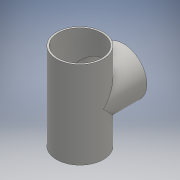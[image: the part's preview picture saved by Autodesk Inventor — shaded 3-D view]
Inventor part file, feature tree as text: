
AUTODESK INVENTOR PART (.ipt)
format: ipt  version: 2016 (Build 200138000, 138)  size: 144,896 bytes
history: native  units: mm
features: extrude x4, sketch x4, projected_geometry x1
ambient origin geometry x8: Origin, YZ Plane, XZ Plane, XY Plane, X Axis, Y Axis, Z Axis, Center Point
bodies: Solid1 (feature_tree)
feature tree (9):
  extrude  "Extrusion1"  Depth=9.52mm
  extrude  "Extrusion2"  Depth=9.52mm
  extrude  "Extrusion3"  Depth=254.0mm TaperAngle=0.0deg
  extrude  "Extrusion4"  Depth=254.0mm TaperAngle=0.0deg
  sketch  "Sketch1"  dims[d0=273.0mm d1=9.52mm]
  sketch  "Sketch2"  dims[d2=508.0mm d3=0.0mm d4=9.52mm]
  sketch  "Sketch3"  dims[d5=273.0mm d6=254.0mm d7=0.0mm]
  sketch  "Sketch4"  dims[d8=254.0mm d9=0.0mm d10=254.0mm d11=0.0mm]
  projected_geometry  "Projected Loop1"
